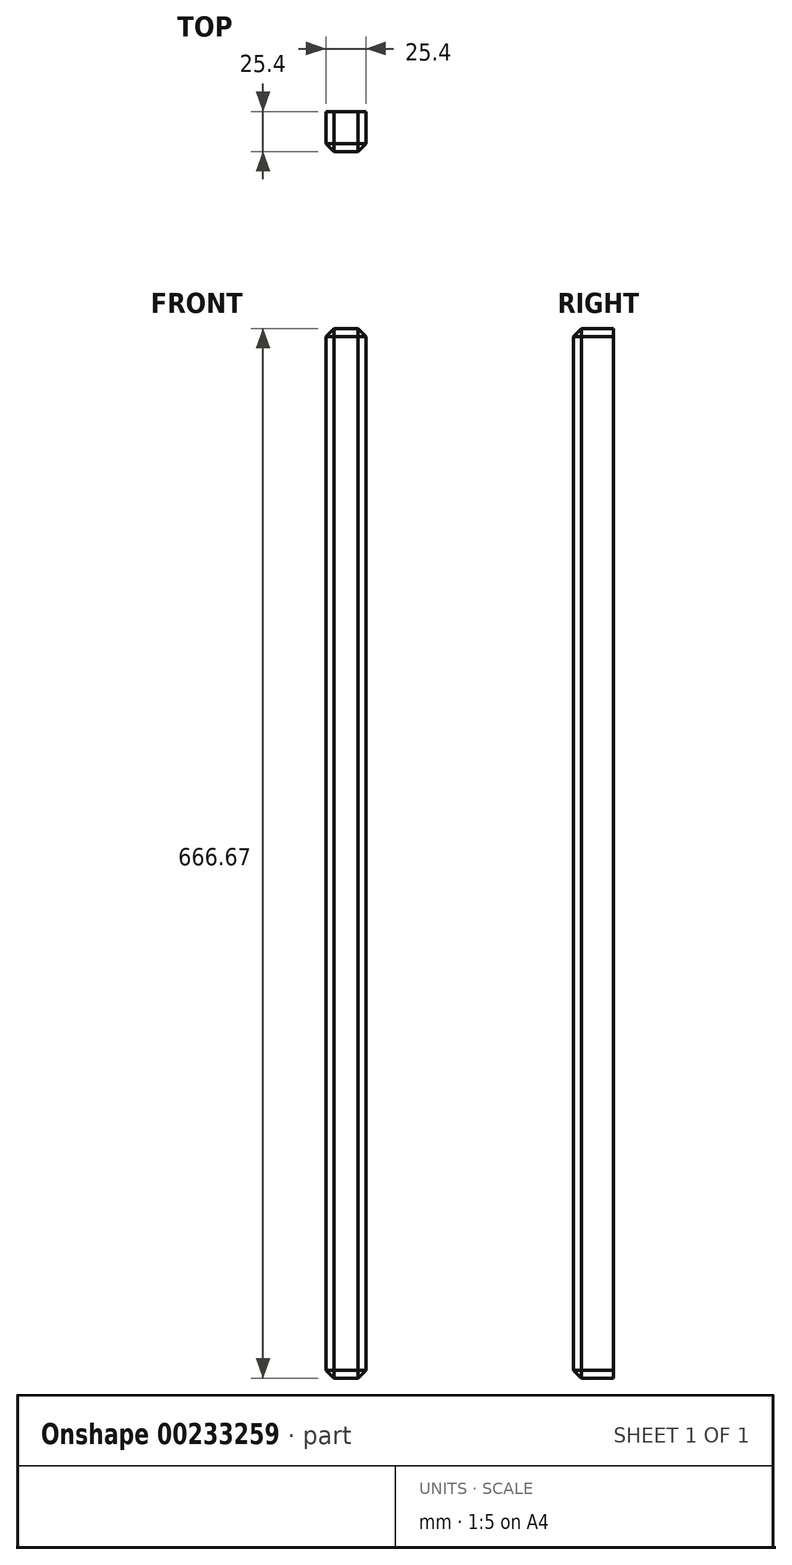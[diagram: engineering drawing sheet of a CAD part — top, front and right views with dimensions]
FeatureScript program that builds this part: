
annotation { "Feature Type Name" : "Feature", "Feature Type Description" : "" }
export const myFeature = defineFeature(function(context is Context, id is Id, definition is map)
    precondition{}
    {
        {
            var Q0;
            Q0=qCreatedBy(makeId("Front.planeOp"),FACE);
            var sketch = newSketch(context, id + "F0", { "sketchPlane" : qUnion([Q0])});
            skLineSegment(sketch, "E0.bottom", {"start": v(-133.37, 171.96) * mm, "end": v(-107.97, 171.96) * mm});
            skLineSegment(sketch, "E0.top", {"start": v(-133.37, -494.7) * mm, "end": v(-107.97, -494.7) * mm});
            skLineSegment(sketch, "E0.left", {"start": v(-133.37, 171.96) * mm, "end": v(-133.37, -494.7) * mm});
            skLineSegment(sketch, "E0.right", {"start": v(-107.97, 171.96) * mm, "end": v(-107.97, -494.7) * mm});
            skSolve(sketch);
        }
        {
            var Q0;
            Q0 = qSketchRegion(id + "F0", true);
            extrude(context, id + "F1", {"entities" : qUnion([Q0]), "depth" : 25.4 * mm});
        }
        {
            var Q0;
            Q0=makeQuery(id+"F1.opExtrude","CAP_EDGE",EDGE,{"disambiguationData":[OSD([sQuery(id+"F0.wireOp",EDGE,"E0.bottom")])],"isStart":false});
            var Q1;
            Q1=makeQuery(id+"F1.opExtrude","SWEPT_EDGE",EDGE,{"disambiguationData":[OSD([sQuery(id+"F0.wireOp",EDGE,"E0.bottom"),sQuery(id+"F0.wireOp",EDGE,"E0.right")])]});
            var Q2;
            Q2=makeQuery(id+"F1.opExtrude","SWEPT_EDGE",EDGE,{"disambiguationData":[OSD([sQuery(id+"F0.wireOp",EDGE,"E0.bottom"),sQuery(id+"F0.wireOp",EDGE,"E0.left")])]});
            var Q3;
            Q3=makeQuery(id+"F1.opExtrude","CAP_FACE",FACE,{"disambiguationData":[OSD([sQuery(id+"F0.wireOp",EDGE,"E0.bottom"),sQuery(id+"F0.wireOp",EDGE,"E0.top"),sQuery(id+"F0.wireOp",EDGE,"E0.left"),sQuery(id+"F0.wireOp",EDGE,"E0.right")])],"isStart":false});
            var Q4;
            Q4=makeQuery(id+"F1.opExtrude","SWEPT_EDGE",EDGE,{"disambiguationData":[OSD([sQuery(id+"F0.wireOp",EDGE,"E0.top"),sQuery(id+"F0.wireOp",EDGE,"E0.left")])]});
            var Q5;
            Q5=makeQuery(id+"F1.opExtrude","SWEPT_EDGE",EDGE,{"disambiguationData":[OSD([sQuery(id+"F0.wireOp",EDGE,"E0.top"),sQuery(id+"F0.wireOp",EDGE,"E0.right")])]});
            chamfer(context, id + "F2", {"entities" : qUnion([Q0, Q1, Q2, Q3, Q4, Q5]), "width" : 5.08 * mm, "tangentPropagation" : true});
        }
    });
